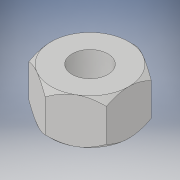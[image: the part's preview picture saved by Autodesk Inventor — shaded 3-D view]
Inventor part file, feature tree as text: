
AUTODESK INVENTOR PART (.ipt)
format: ipt  version: 2019 (Build 230136000, 136)  size: 136,704 bytes
history: native  units: in
note: dims shown in document units (in); Inventor stores cm internally (conversion verified against a paired STEP export)
features: extrude x4, sketch x4
ambient origin geometry x8: Origin, YZ Plane, XZ Plane, XY Plane, X Axis, Y Axis, Z Axis, Center Point
bodies: Solid1 (feature_tree)
feature tree (8):
  extrude  "Extrusion1"  Depth=0.5in TaperAngle=0.0deg
  extrude  "Extrusion2"  Depth=0.5in TaperAngle=45.0deg
  extrude  "Extrusion3"  Depth=0.5in TaperAngle=0.0deg
  extrude  "Extrusion4"  [1 undecoded]
  sketch  "Sketch1"  dims[d2=1.0in d3=0.5in d4=0.0in]
  sketch  "Sketch2"  dims[d5=0.5in d6=45.0deg d7=0.5in d8=45.0deg]
  sketch  "Sketch3"  dims[d9=0.4in d10=0.5in d11=0.0in]
  sketch  "Sketch4"
note: 1 required parameter value undecoded (feature->parameter linkage not recoverable at this tier; creation-order binding heuristic only, values carry confidence <= 0.55)
